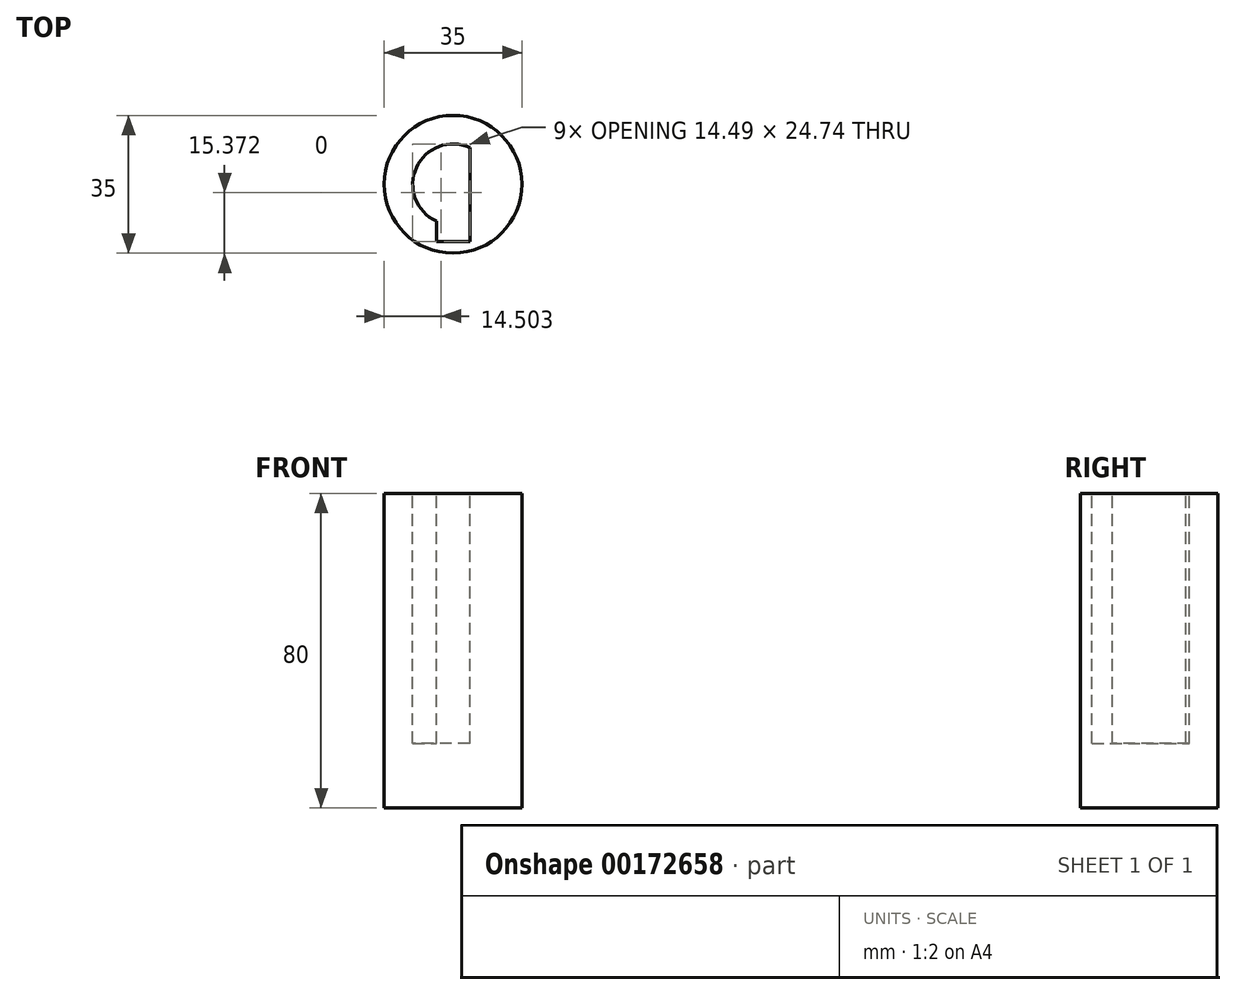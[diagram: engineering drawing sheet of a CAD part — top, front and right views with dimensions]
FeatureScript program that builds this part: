
annotation { "Feature Type Name" : "Feature", "Feature Type Description" : "" }
export const myFeature = defineFeature(function(context is Context, id is Id, definition is map)
    precondition{}
    {
        {
            var Q0;
            Q0=qCreatedBy(makeId("Top.planeOp"),FACE);
            var sketch = newSketch(context, id + "F0", { "sketchPlane" : qUnion([Q0])});
            skCircle(sketch, "E0", {"center": v(0, 0) * mm, "radius": 17.5 * mm});
            skSolve(sketch);
        }
        {
            var Q0;
            Q0=makeQuery(id+"F0.imprint","IMPRINT",FACE,{"disambiguationData":[TD([[makeQuery(id+"F0.imprint","IMPRINT",EDGE,{"derivedFrom":sQuery(id+"F0.wireOp",EDGE,"E0")}),1.0]])]});
            extrude(context, id + "F1", {"entities" : qUnion([Q0]), "depth" : 80 * mm});
        }
        {
            var Q0;
            Q0=makeQuery(id+"F1.opExtrude","CAP_FACE",FACE,{"disambiguationData":[OSD([sQuery(id+"F0.wireOp",EDGE,"E0")])],"isStart":false});
            var sketch = newSketch(context, id + "F2", { "sketchPlane" : qUnion([Q0])});
            skCircle(sketch, "E1", {"center": v(0, 0) * mm, "radius": 10.25 * mm});
            skLineSegment(sketch, "E2.bottom", {"start": v(4.25, -14.5) * mm, "end": v(-4.25, -14.5) * mm});
            skLineSegment(sketch, "E2.top", {"start": v(4.25, 14.5) * mm, "end": v(-4.25, 14.5) * mm});
            skLineSegment(sketch, "E2.left", {"start": v(4.25, -14.5) * mm, "end": v(4.25, 14.5) * mm});
            skLineSegment(sketch, "E2.right", {"start": v(-4.25, -14.5) * mm, "end": v(-4.25, 14.5) * mm});
            skSolve(sketch);
        }
        {
            var Q0;
            {var subQ5=sQuery(id+"F2.wireOp",EDGE,"E2.bottom");Q0=makeQuery(id+"F2.imprint","IMPRINT",FACE,{"disambiguationData":[TD([[makeQuery(id+"F2.imprint","IMPRINT",EDGE,{"derivedFrom":subQ5}),-1.0]])]});}
            var Q1;
            {var subQ0=sQuery(id+"F2.wireOp",EDGE,"E2.left");var subQ1=sQuery(id+"F2.wireOp",EDGE,"E1");var subQ2=makeQuery(id+"F2.imprint","INTERSECT",VERTEX,{"disambiguationData":[OD(0.0)],"derivedFrom":[subQ1,subQ0]});Q1=makeQuery(id+"F2.imprint","IMPRINT",FACE,{"disambiguationData":[TD([[makeQuery(id+"F2.imprint","IMPRINT",EDGE,{"disambiguationData":[TD([[subQ2,1.0]])],"derivedFrom":subQ1}),1.0]])]});}
            var Q2;
            {var subQ0=sQuery(id+"F2.wireOp",EDGE,"E2.right");var subQ1=sQuery(id+"F2.wireOp",EDGE,"E1");var subQ2=makeQuery(id+"F2.imprint","INTERSECT",VERTEX,{"disambiguationData":[OD(0.0)],"derivedFrom":[subQ1,subQ0]});Q2=makeQuery(id+"F2.imprint","IMPRINT",FACE,{"disambiguationData":[TD([[makeQuery(id+"F2.imprint","IMPRINT",EDGE,{"disambiguationData":[TD([[subQ2,1.0]])],"derivedFrom":subQ1}),1.0]])]});}
            var Q3;
            {var subQ0=sQuery(id+"F2.wireOp",EDGE,"E2.right");var subQ1=sQuery(id+"F2.wireOp",EDGE,"E1");var subQ2=makeQuery(id+"F2.imprint","INTERSECT",VERTEX,{"disambiguationData":[OD(0.0)],"derivedFrom":[subQ1,subQ0]});Q3=makeQuery(id+"F2.imprint","IMPRINT",FACE,{"disambiguationData":[TD([[makeQuery(id+"F2.imprint","IMPRINT",EDGE,{"disambiguationData":[TD([[subQ2,-1.0]])],"derivedFrom":subQ1}),1.0]])]});}
            extrude(context, id + "F3", {"entities" : qUnion([Q0, Q1, Q2, Q3]), "operationType" : NewBodyOperationType.REMOVE, "oppositeDirection" : true, "depth" : 63.5 * mm});
        }
    });
